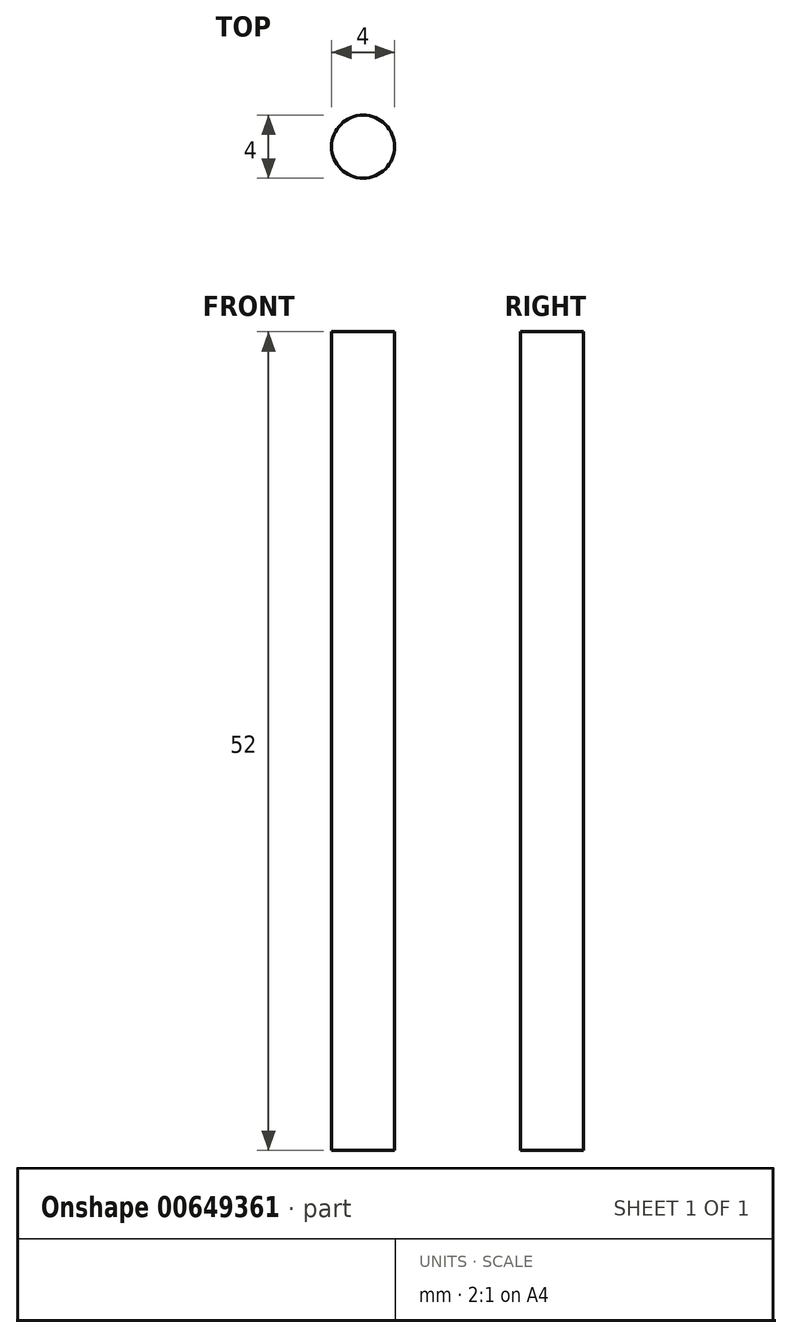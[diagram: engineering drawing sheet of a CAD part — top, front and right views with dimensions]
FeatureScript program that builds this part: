
annotation { "Feature Type Name" : "Feature", "Feature Type Description" : "" }
export const myFeature = defineFeature(function(context is Context, id is Id, definition is map)
    precondition{}
    {
        {
            var Q0;
            Q0=qCreatedBy(makeId("Top.planeOp"),FACE);
            var sketch = newSketch(context, id + "F0", { "sketchPlane" : qUnion([Q0])});
            skCircle(sketch, "E0", {"center": v(0, 0) * mm, "radius": 2 * mm});
            skSolve(sketch);
        }
        {
            var Q0;
            Q0 = qSketchRegion(id + "F0", true);
            extrude(context, id + "F1", {"entities" : qUnion([Q0]), "depth" : 52 * mm, "offsetDistance" : 25 * mm});
        }
    });
